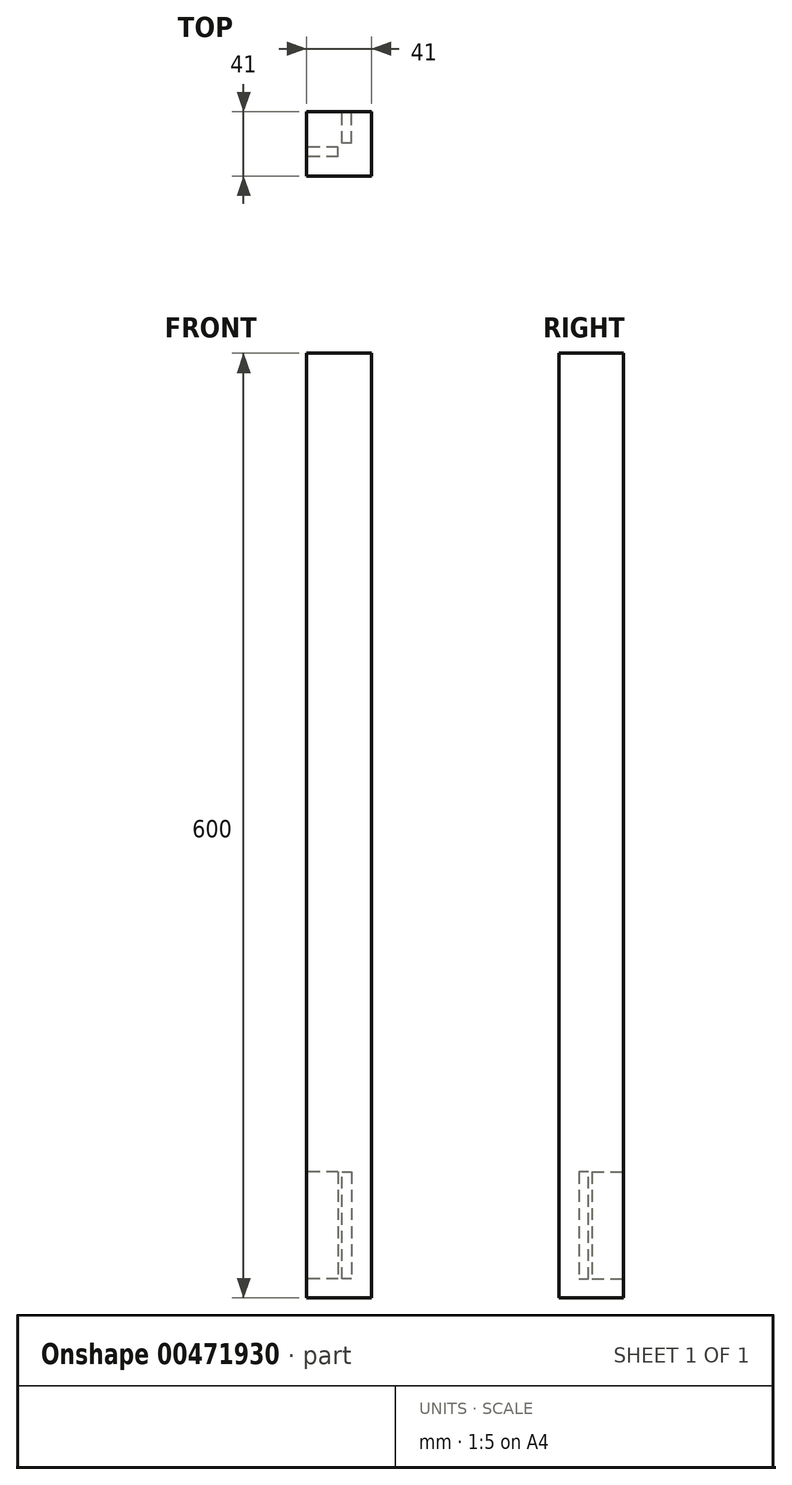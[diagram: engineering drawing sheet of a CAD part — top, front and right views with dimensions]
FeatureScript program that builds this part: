
annotation { "Feature Type Name" : "Feature", "Feature Type Description" : "" }
export const myFeature = defineFeature(function(context is Context, id is Id, definition is map)
    precondition{}
    {
        {
            var Q0;
            Q0=qCreatedBy(makeId("Top.planeOp"),FACE);
            var sketch = newSketch(context, id + "F0", { "sketchPlane" : qUnion([Q0])});
            skLineSegment(sketch, "E0", {"start": v(-15.72, 17) * mm, "end": v(25.28, 17) * mm});
            skLineSegment(sketch, "E1", {"start": v(25.28, 17) * mm, "end": v(25.28, -24) * mm});
            skLineSegment(sketch, "E2", {"start": v(25.28, -24) * mm, "end": v(-15.72, -24) * mm});
            skLineSegment(sketch, "E3", {"start": v(-15.72, -24) * mm, "end": v(-15.72, 17) * mm});
            skSolve(sketch);
        }
        {
            var Q0;
            Q0=makeQuery(id+"F0.imprint","IMPRINT",FACE,{"disambiguationData":[TD([[makeQuery(id+"F0.imprint","IMPRINT",EDGE,{"derivedFrom":sQuery(id+"F0.wireOp",EDGE,"E0")}),-1.0]])]});
            extrude(context, id + "F1", {"entities" : qUnion([Q0]), "depth" : 600 * mm});
        }
        {
            var Q0;
            Q0=makeQuery(id+"F1.opExtrude","SWEPT_FACE",FACE,{"disambiguationData":[OSD([sQuery(id+"F0.wireOp",EDGE,"E3")])]});
            var sketch = newSketch(context, id + "F2", { "sketchPlane" : qUnion([Q0])});
            skLineSegment(sketch, "E4", {"start": v(11.5, 12) * mm, "end": v(5.5, 12) * mm});
            skLineSegment(sketch, "E5", {"start": v(5.5, 12) * mm, "end": v(5.5, 80) * mm});
            skLineSegment(sketch, "E6", {"start": v(5.5, 80) * mm, "end": v(11.5, 80) * mm});
            skLineSegment(sketch, "E7", {"start": v(11.5, 80) * mm, "end": v(11.5, 12) * mm});
            skSolve(sketch);
        }
        {
            var Q0;
            Q0 = qSketchRegion(id + "F2", true);
            extrude(context, id + "F3", {"entities" : qUnion([Q0]), "operationType" : NewBodyOperationType.REMOVE, "oppositeDirection" : true, "depth" : 20 * mm});
        }
        {
            var Q0;
            Q0=makeQuery(id+"F1.opExtrude","SWEPT_FACE",FACE,{"disambiguationData":[OSD([sQuery(id+"F0.wireOp",EDGE,"E0")])]});
            var sketch = newSketch(context, id + "F4", { "sketchPlane" : qUnion([Q0])});
            skLineSegment(sketch, "E8", {"start": v(-12.78, 12) * mm, "end": v(-6.78, 12) * mm});
            skLineSegment(sketch, "E9", {"start": v(-6.78, 12) * mm, "end": v(-6.78, 80) * mm});
            skLineSegment(sketch, "E10", {"start": v(-6.78, 80) * mm, "end": v(-12.78, 80) * mm});
            skLineSegment(sketch, "E11", {"start": v(-12.78, 80) * mm, "end": v(-12.78, 12) * mm});
            skSolve(sketch);
        }
        {
            var Q0;
            Q0 = qSketchRegion(id + "F4", true);
            extrude(context, id + "F5", {"entities" : qUnion([Q0]), "operationType" : NewBodyOperationType.REMOVE, "oppositeDirection" : true, "depth" : 20 * mm});
        }
    });
